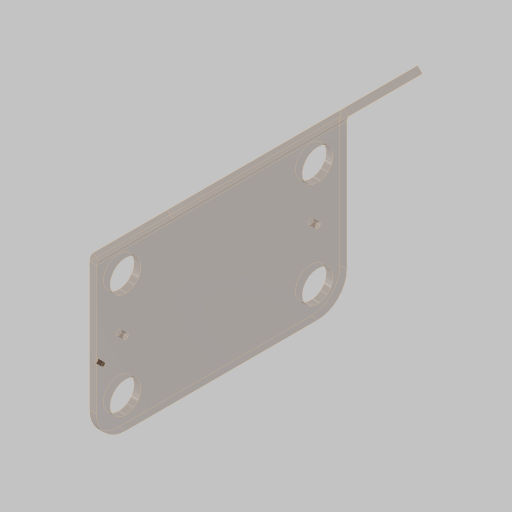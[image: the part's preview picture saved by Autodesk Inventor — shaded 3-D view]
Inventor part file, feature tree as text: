
AUTODESK INVENTOR PART (.ipt)
format: ipt  version: 2023.5 (Build 275446000, 446)  size: 156,672 bytes
history: native  units: in
note: dims shown in document units (in); Inventor stores cm internally (conversion verified against a paired STEP export)
features: sketch x3, sheet_metal_op x3, hole x2, extrude x1, other x1
ambient origin geometry x8: Origin, YZ Plane, XZ Plane, XY Plane, X Axis, Y Axis, Z Axis, Center Point
bodies: Solid1 (feature_tree)
feature tree (10):
  sketch  "Sketch1"  dims[d0=1.125in d2=12.0in]
  extrude  "Extrusion1"  Depth=12.0in
  hole  "Hole1"  [1 undecoded]
  sheet_metal_op  "Flange1"
  hole  "Hole2"  [1 undecoded]
  sketch  "Sketch2"  dims[d3=4.5in d4=3.0in]
  other  "Plate1"
  sheet_metal_op  "Bend1"
  sheet_metal_op  "Corner1"
  sketch  "Sketch3"  dims[d6=0.25in d7=0.5in d8=3.8356in d9=0.25in d10=0.0in d11=0.201in d12=0.38in d13=0.385in d14=0.25in d15=0.5635in d16=1.0in d17=0.8108in d18=0.25in d19=0.25in d20=0.125in d21=0.5in d22=0.25in d23=4.0in d24=45.0deg d25=0.25in d26=1.0in d27=0.25in d28=0.25in d29=0.25in d30=2.5in d31=0.13in d32=0.328in d33=0.332in d34=0.25in d35=0.5635in d36=1.0in d37=0.8108in]
note: 2 required parameter values undecoded (feature->parameter linkage not recoverable at this tier; creation-order binding heuristic only, values carry confidence <= 0.55)
